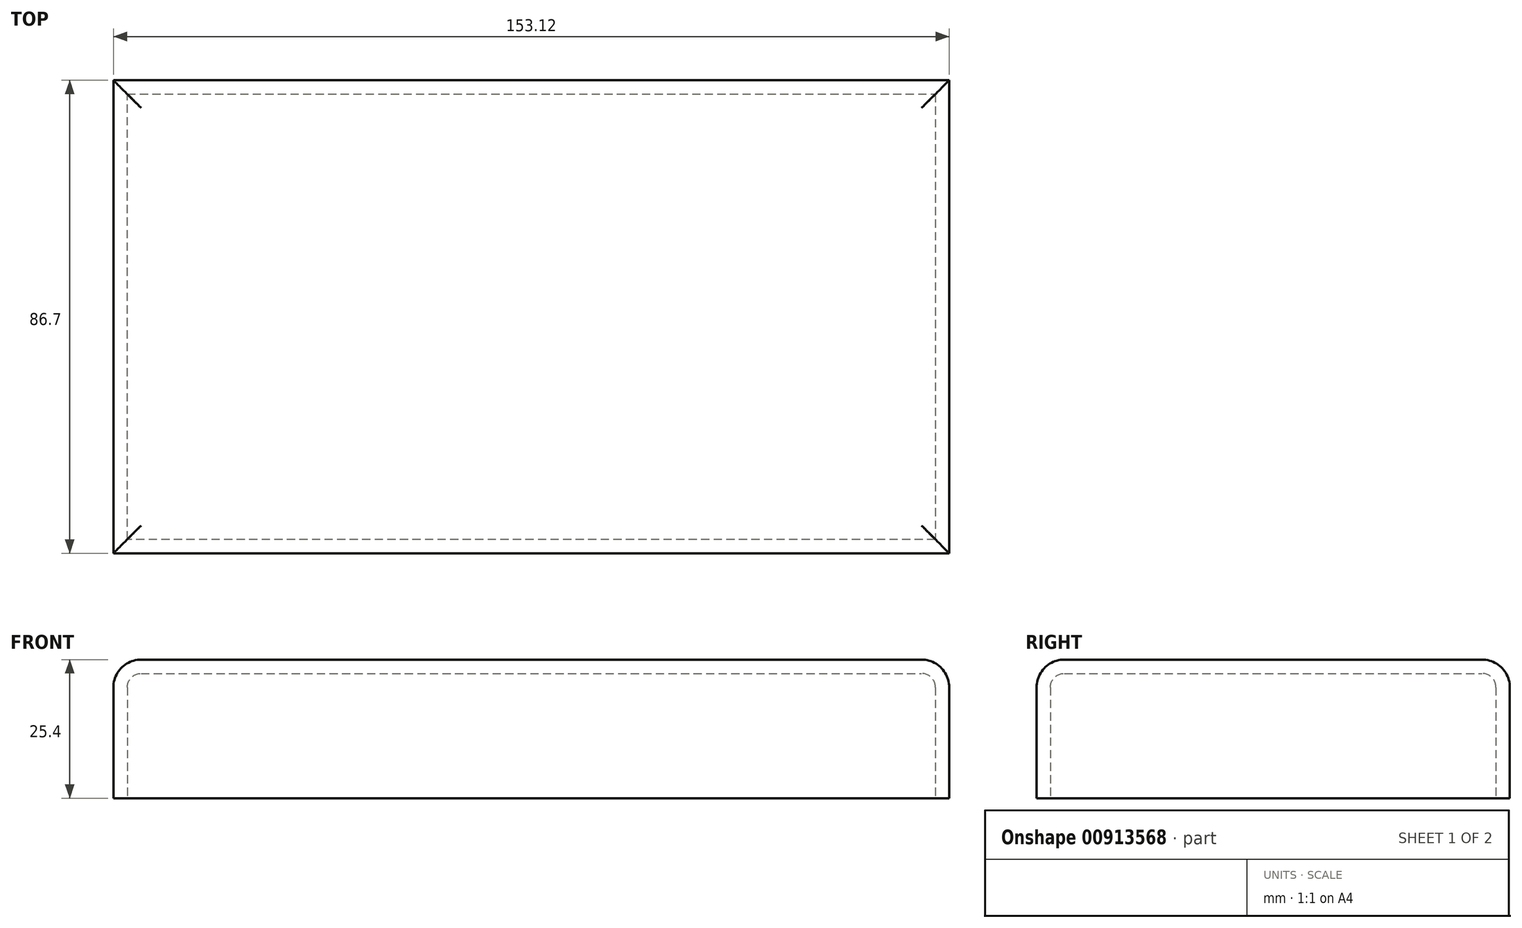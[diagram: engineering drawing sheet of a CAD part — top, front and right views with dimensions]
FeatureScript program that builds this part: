
annotation { "Feature Type Name" : "Feature", "Feature Type Description" : "" }
export const myFeature = defineFeature(function(context is Context, id is Id, definition is map)
    precondition{}
    {
        {
            var Q0;
            Q0=qCreatedBy(makeId("Top.planeOp"),FACE);
            var sketch = newSketch(context, id + "F0", { "sketchPlane" : qUnion([Q0])});
            skLineSegment(sketch, "E0", {"start": v(0, 0) * mm, "end": v(153.12, 0) * mm});
            skLineSegment(sketch, "E1", {"start": v(153.12, 0) * mm, "end": v(153.12, -86.7) * mm});
            skLineSegment(sketch, "E2", {"start": v(153.12, -86.7) * mm, "end": v(0, -86.7) * mm});
            skLineSegment(sketch, "E3", {"start": v(0, -86.7) * mm, "end": v(0, 0) * mm});
            skSolve(sketch);
        }
        {
            var Q0;
            Q0=makeQuery(id+"F0.imprint","IMPRINT",FACE,{"disambiguationData":[TD([[makeQuery(id+"F0.imprint","IMPRINT",EDGE,{"derivedFrom":sQuery(id+"F0.wireOp",EDGE,"E0")}),-1.0]])]});
            extrude(context, id + "F1", {"entities" : qUnion([Q0]), "depth" : 25.4 * mm, "offsetDistance" : 25.4 * mm});
        }
        {
            var Q0;
            Q0=makeQuery(id+"F1.opExtrude","CAP_EDGE",EDGE,{"disambiguationData":[OSD([sQuery(id+"F0.wireOp",EDGE,"E3")])],"isStart":false});
            var Q1;
            Q1=makeQuery(id+"F1.opExtrude","CAP_EDGE",EDGE,{"disambiguationData":[OSD([sQuery(id+"F0.wireOp",EDGE,"E2")])],"isStart":false});
            var Q2;
            Q2=makeQuery(id+"F1.opExtrude","CAP_EDGE",EDGE,{"disambiguationData":[OSD([sQuery(id+"F0.wireOp",EDGE,"E0")])],"isStart":false});
            var Q3;
            Q3=makeQuery(id+"F1.opExtrude","CAP_EDGE",EDGE,{"disambiguationData":[OSD([sQuery(id+"F0.wireOp",EDGE,"E1")])],"isStart":false});
            fillet(context, id + "F2", {"entities" : qUnion([Q0, Q1, Q2, Q3]), "radius" : 5.08 * mm, "tangentPropagation" : true, "allowEdgeOverflow" : false});
        }
        {
            var Q0;
            Q0=makeQuery(id+"F1.opExtrude","CAP_FACE",FACE,{"disambiguationData":[OSD([sQuery(id+"F0.wireOp",EDGE,"E0"),sQuery(id+"F0.wireOp",EDGE,"E1"),sQuery(id+"F0.wireOp",EDGE,"E2"),sQuery(id+"F0.wireOp",EDGE,"E3")])],"isStart":true});
            shell(context, id + "F3", {"entities" : qUnion([Q0]), "thickness" : 2.54 * mm});
        }
    });
